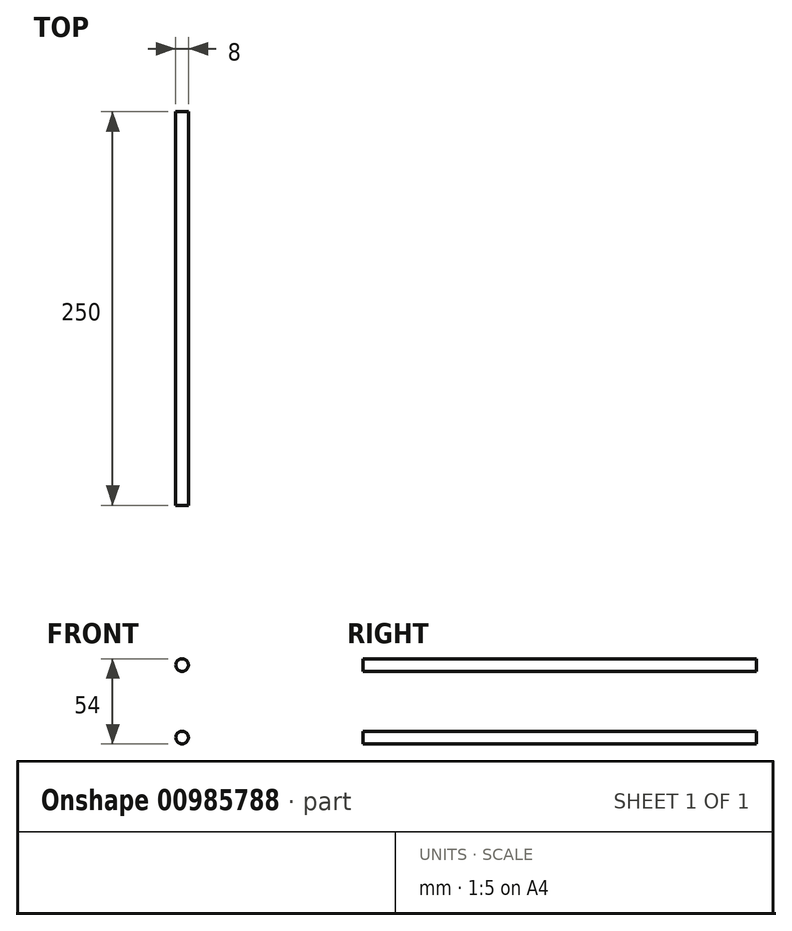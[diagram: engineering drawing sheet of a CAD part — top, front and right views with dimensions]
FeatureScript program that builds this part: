
annotation { "Feature Type Name" : "Feature", "Feature Type Description" : "" }
export const myFeature = defineFeature(function(context is Context, id is Id, definition is map)
    precondition{}
    {
        {
            var Q0;
            Q0=qCreatedBy(makeId("Front.planeOp"),FACE);
            var sketch = newSketch(context, id + "F0", { "sketchPlane" : qUnion([Q0])});
            skCircle(sketch, "E0", {"center": v(0, 0) * mm, "radius": 4 * mm});
            skCircle(sketch, "E1", {"center": v(0, 46) * mm, "radius": 4 * mm});
            skSolve(sketch);
        }
        {
            var Q0;
            Q0 = qSketchRegion(id + "F0", true);
            extrude(context, id + "F1", {"entities" : qUnion([Q0]), "depth" : 250 * mm, "offsetDistance" : 25 * mm});
        }
    });
